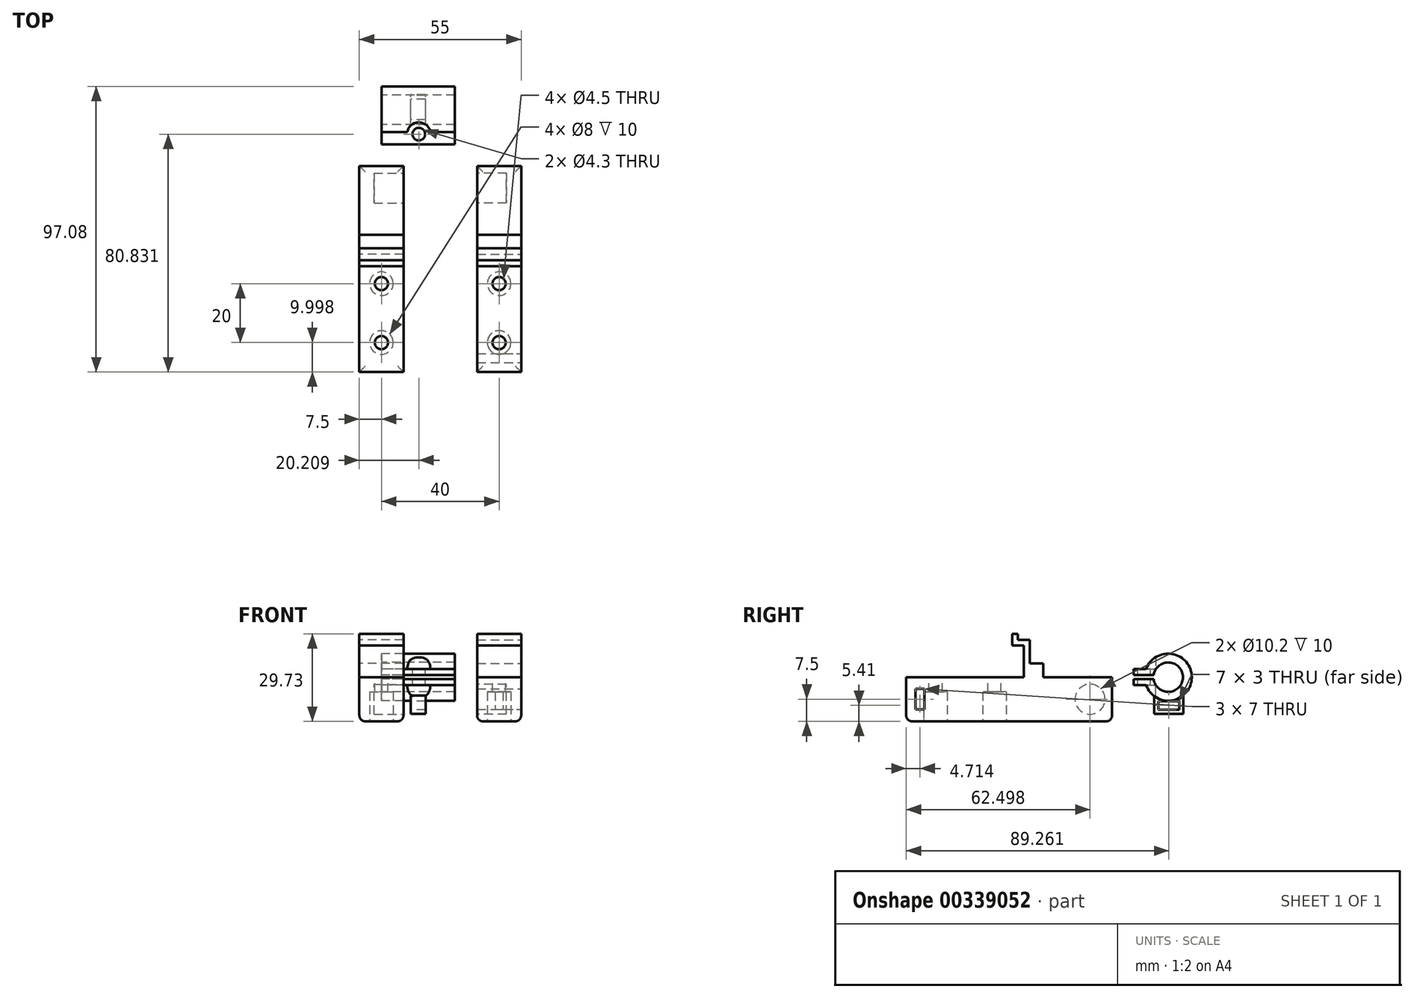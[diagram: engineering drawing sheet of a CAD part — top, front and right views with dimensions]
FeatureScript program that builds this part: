
annotation { "Feature Type Name" : "Feature", "Feature Type Description" : "" }
export const myFeature = defineFeature(function(context is Context, id is Id, definition is map)
    precondition{}
    {
        {
            var Q0;
            Q0=qCreatedBy(makeId("Top.planeOp"),FACE);
            var sketch = newSketch(context, id + "F0", { "sketchPlane" : qUnion([Q0])});
            skLineSegment(sketch, "E0", {"start": v(120.64, 20) * mm, "end": v(-98.83, 20) * mm, "construction": true});
            skLineSegment(sketch, "E1", {"start": v(-113.57, -20) * mm, "end": v(119.85, -20) * mm, "construction": true});
            skLineSegment(sketch, "E2", {"start": v(-15.81, 35.6) * mm, "end": v(120.22, 35.6) * mm, "construction": true});
            skLineSegment(sketch, "E3", {"start": v(0, 0) * mm, "end": v(121.2, 0) * mm, "construction": true});
            skSolve(sketch);
        }
        {
            var Q0;
            Q0=qCreatedBy(makeId("Right.planeOp"),FACE);
            var sketch = newSketch(context, id + "F1", { "sketchPlane" : qUnion([Q0])});
            skLineSegment(sketch, "E4", {"start": v(13.49, 0) * mm, "end": v(-26.51, 0) * mm});
            skLineSegment(sketch, "E5", {"start": v(-26.51, 0) * mm, "end": v(-26.51, -15) * mm});
            skLineSegment(sketch, "E6", {"start": v(-26.51, -15) * mm, "end": v(18.49, -15) * mm});
            skLineSegment(sketch, "E7", {"start": v(13.49, 10.73) * mm, "end": v(13.49, 0) * mm});
            skLineSegment(sketch, "E8", {"start": v(43.49, -15) * mm, "end": v(43.49, 0) * mm});
            skLineSegment(sketch, "E9", {"start": v(43.49, 0) * mm, "end": v(20.14, 0) * mm});
            skLineSegment(sketch, "E10", {"start": v(13.49, 10.73) * mm, "end": v(9.49, 10.73) * mm});
            skLineSegment(sketch, "E11", {"start": v(9.49, 10.73) * mm, "end": v(9.49, 14.73) * mm});
            skLineSegment(sketch, "E12", {"start": v(9.49, 14.73) * mm, "end": v(11.49, 14.73) * mm});
            skLineSegment(sketch, "E13", {"start": v(11.49, 14.73) * mm, "end": v(11.49, 12.73) * mm});
            skLineSegment(sketch, "E14", {"start": v(18.49, -15) * mm, "end": v(43.49, -15) * mm});
            skLineSegment(sketch, "E15", {"start": v(20.14, 0) * mm, "end": v(20.14, 4.7) * mm});
            skLineSegment(sketch, "E16", {"start": v(20.14, 4.7) * mm, "end": v(15.49, 4.7) * mm});
            skPoint(sketch, "E17.orphan", {"position": v(15.49, 0) * mm});
            skPoint(sketch, "E18.end.orphan", {"position": v(13.49, 21.47) * mm});
            skLineSegment(sketch, "E19", {"start": v(15.49, 4.7) * mm, "end": v(15.49, 12.7) * mm});
            skPoint(sketch, "E20.end.orphan", {"position": v(13.49, 12) * mm});
            skLineSegment(sketch, "E21", {"start": v(15.49, 12.7) * mm, "end": v(11.49, 12.73) * mm});
            skSolve(sketch);
        }
        {
            var Q0;
            Q0=makeQuery(id+"F1.imprint","IMPRINT",FACE,{"disambiguationData":[TD([[makeQuery(id+"F1.imprint","IMPRINT",EDGE,{"derivedFrom":sQuery(id+"F1.wireOp",EDGE,"E4")}),1.0]])]});
            var Q1;
            {var subQ0=sQuery(id+"F1.wireOp",EDGE,"E10");Q1=makeQuery(id+"F1.imprint","IMPRINT",FACE,{"disambiguationData":[TD([[makeQuery(id+"F1.imprint","IMPRINT",EDGE,{"derivedFrom":subQ0}),-1.0]])]});}
            extrude(context, id + "F2", {"entities" : qUnion([Q0, Q1]), "endBound" : BoundingType.SYMMETRIC, "depth" : 15 * mm});
        }
        {
            var Q0;
            Q0=makeQuery(id+"F2.opExtrude","CAP_FACE",FACE,{"disambiguationData":[OSD([sQuery(id+"F1.wireOp",EDGE,"E4"),sQuery(id+"F1.wireOp",EDGE,"E5"),sQuery(id+"F1.wireOp",EDGE,"E6"),sQuery(id+"F1.wireOp",EDGE,"E7"),sQuery(id+"F1.wireOp",EDGE,"E8"),sQuery(id+"F1.wireOp",EDGE,"E9"),sQuery(id+"F1.wireOp",EDGE,"E10"),sQuery(id+"F1.wireOp",EDGE,"E11"),sQuery(id+"F1.wireOp",EDGE,"E12"),sQuery(id+"F1.wireOp",EDGE,"E13"),sQuery(id+"F1.wireOp",EDGE,"E14"),sQuery(id+"F1.wireOp",EDGE,"E15"),sQuery(id+"F1.wireOp",EDGE,"E16"),sQuery(id+"F1.wireOp",EDGE,"E19"),sQuery(id+"F1.wireOp",EDGE,"E21")])],"isStart":false});
            var sketch = newSketch(context, id + "F3", { "sketchPlane" : qUnion([Q0])});
            skCircle(sketch, "E22", {"center": v(35.99, -7.5) * mm, "radius": 5.1 * mm});
            skSolve(sketch);
        }
        {
            var Q0;
            Q0=makeQuery(id+"F3.imprint","IMPRINT",FACE,{"disambiguationData":[TD([[makeQuery(id+"F3.imprint","IMPRINT",EDGE,{"derivedFrom":sQuery(id+"F3.wireOp",EDGE,"E22")}),1.0]])]});
            extrude(context, id + "F4", {"entities" : qUnion([Q0]), "operationType" : NewBodyOperationType.REMOVE, "oppositeDirection" : true, "depth" : 10 * mm});
        }
        {
            var Q0;
            Q0=qCreatedBy(makeId("Right.planeOp"),FACE);
            cPlane(context, id + "F5", {"entities" : qUnion([Q0]), "cplaneType" : CPlaneType.OFFSET, "offset" : 20 * mm, "width" : 150 * mm, "height" : 150 * mm});
        }
        {
            var Q0;
            Q0=makeQuery(id+"F2.opExtrude","SWEPT_BODY",BODY,{"disambiguationData":[OSD([sQuery(id+"F1.wireOp",EDGE,"E4"),sQuery(id+"F1.wireOp",EDGE,"E5"),sQuery(id+"F1.wireOp",EDGE,"E6"),sQuery(id+"F1.wireOp",EDGE,"E7"),sQuery(id+"F1.wireOp",EDGE,"E8"),sQuery(id+"F1.wireOp",EDGE,"E9"),sQuery(id+"F1.wireOp",EDGE,"E10"),sQuery(id+"F1.wireOp",EDGE,"E11"),sQuery(id+"F1.wireOp",EDGE,"E12"),sQuery(id+"F1.wireOp",EDGE,"E13"),sQuery(id+"F1.wireOp",EDGE,"E14"),sQuery(id+"F1.wireOp",EDGE,"E15"),sQuery(id+"F1.wireOp",EDGE,"E16"),sQuery(id+"F1.wireOp",EDGE,"E19"),sQuery(id+"F1.wireOp",EDGE,"E21")])]});
            var Q1;
            Q1=qCreatedBy(id+"F5.planeOp",FACE);
            mirror(context, id + "F6", {"entities" : qUnion([Q0]), "mirrorPlane" : qUnion([Q1])});
        }
        {
            var Q0;
            Q0=makeQuery(id+"F6.opPattern","COPY",FACE,{"derivedFrom":makeQuery(id+"F2.opExtrude","CAP_FACE",FACE,{"disambiguationData":[OSD([sQuery(id+"F1.wireOp",EDGE,"E4"),sQuery(id+"F1.wireOp",EDGE,"E5"),sQuery(id+"F1.wireOp",EDGE,"E6"),sQuery(id+"F1.wireOp",EDGE,"E7"),sQuery(id+"F1.wireOp",EDGE,"E8"),sQuery(id+"F1.wireOp",EDGE,"E9"),sQuery(id+"F1.wireOp",EDGE,"E10"),sQuery(id+"F1.wireOp",EDGE,"E11"),sQuery(id+"F1.wireOp",EDGE,"E12"),sQuery(id+"F1.wireOp",EDGE,"E13"),sQuery(id+"F1.wireOp",EDGE,"E14"),sQuery(id+"F1.wireOp",EDGE,"E15"),sQuery(id+"F1.wireOp",EDGE,"E16"),sQuery(id+"F1.wireOp",EDGE,"E19"),sQuery(id+"F1.wireOp",EDGE,"E21")])],"isStart":true}),"instanceName":"1"});
            var sketch = newSketch(context, id + "F7", { "sketchPlane" : qUnion([Q0])});
            skLineSegment(sketch, "E23.bottom", {"start": v(-20.3, -4) * mm, "end": v(-23.3, -4) * mm});
            skLineSegment(sketch, "E23.top", {"start": v(-20.3, -11) * mm, "end": v(-23.3, -11) * mm});
            skLineSegment(sketch, "E23.left", {"start": v(-20.3, -4) * mm, "end": v(-20.3, -11) * mm});
            skLineSegment(sketch, "E23.right", {"start": v(-23.3, -4) * mm, "end": v(-23.3, -11) * mm});
            skSolve(sketch);
        }
        {
            var Q0;
            Q0=makeQuery(id+"F7.imprint","IMPRINT",FACE,{"disambiguationData":[TD([[makeQuery(id+"F7.imprint","IMPRINT",EDGE,{"derivedFrom":sQuery(id+"F7.wireOp",EDGE,"E23.bottom")}),1.0]])]});
            extrude(context, id + "F8", {"entities" : qUnion([Q0]), "operationType" : NewBodyOperationType.REMOVE, "endBound" : BoundingType.UP_TO_NEXT, "oppositeDirection" : true, "depth" : 25 * mm});
        }
        {
            var Q0;
            Q0=makeQuery(id+"F8.boolean.opBoolean","COPY",EDGE,{"derivedFrom":makeQuery(id+"F8.opExtrude","CAP_EDGE",EDGE,{"disambiguationData":[OSD([sQuery(id+"F7.wireOp",EDGE,"E23.right")])],"isStart":true})});
            var Q1;
            Q1=makeQuery(id+"F8.boolean.opBoolean","COPY",EDGE,{"derivedFrom":makeQuery(id+"F8.opExtrude","TWEAK_EDGE",EDGE,{"derivedFrom":[makeQuery(id+"F6.opPattern","COPY",FACE,{"derivedFrom":makeQuery(id+"F2.opExtrude","CAP_FACE",FACE,{"disambiguationData":[OSD([sQuery(id+"F1.wireOp",EDGE,"E4"),sQuery(id+"F1.wireOp",EDGE,"E5"),sQuery(id+"F1.wireOp",EDGE,"E6"),sQuery(id+"F1.wireOp",EDGE,"E7"),sQuery(id+"F1.wireOp",EDGE,"E8"),sQuery(id+"F1.wireOp",EDGE,"E9"),sQuery(id+"F1.wireOp",EDGE,"E10"),sQuery(id+"F1.wireOp",EDGE,"E11"),sQuery(id+"F1.wireOp",EDGE,"E12"),sQuery(id+"F1.wireOp",EDGE,"E13"),sQuery(id+"F1.wireOp",EDGE,"E14"),sQuery(id+"F1.wireOp",EDGE,"E15"),sQuery(id+"F1.wireOp",EDGE,"E16"),sQuery(id+"F1.wireOp",EDGE,"E19"),sQuery(id+"F1.wireOp",EDGE,"E21")])],"isStart":false}),"instanceName":"1"}),makeQuery(id+"F7.imprint","IMPRINT",EDGE,{"derivedFrom":sQuery(id+"F7.wireOp",EDGE,"E23.right")})]})});
            var Q2;
            Q2=makeQuery(id+"F6.opPattern","COPY",EDGE,{"derivedFrom":makeQuery(id+"F2.opExtrude","CAP_EDGE",EDGE,{"disambiguationData":[OSD([sQuery(id+"F1.wireOp",EDGE,"E6"),sQuery(id+"F1.wireOp",EDGE,"E14")])],"isStart":false}),"instanceName":"1"});
            var Q3;
            Q3=makeQuery(id+"F6.opPattern","COPY",EDGE,{"derivedFrom":makeQuery(id+"F2.opExtrude","CAP_EDGE",EDGE,{"disambiguationData":[OSD([sQuery(id+"F1.wireOp",EDGE,"E6"),sQuery(id+"F1.wireOp",EDGE,"E14")])],"isStart":true}),"instanceName":"1"});
            var Q4;
            Q4=makeQuery(id+"F2.opExtrude","CAP_EDGE",EDGE,{"disambiguationData":[OSD([sQuery(id+"F1.wireOp",EDGE,"E6"),sQuery(id+"F1.wireOp",EDGE,"E14")])],"isStart":true});
            var Q5;
            Q5=makeQuery(id+"F2.opExtrude","CAP_EDGE",EDGE,{"disambiguationData":[OSD([sQuery(id+"F1.wireOp",EDGE,"E6"),sQuery(id+"F1.wireOp",EDGE,"E14")])],"isStart":false});
            var Q6;
            Q6=makeQuery(id+"F6.opPattern","COPY",EDGE,{"derivedFrom":makeQuery(id+"F2.opExtrude","SWEPT_EDGE",EDGE,{"disambiguationData":[OSD([sQuery(id+"F1.wireOp",EDGE,"E5"),sQuery(id+"F1.wireOp",EDGE,"E6")])]}),"instanceName":"1"});
            var Q7;
            Q7=makeQuery(id+"F2.opExtrude","SWEPT_EDGE",EDGE,{"disambiguationData":[OSD([sQuery(id+"F1.wireOp",EDGE,"E5"),sQuery(id+"F1.wireOp",EDGE,"E6")])]});
            var Q8;
            Q8=makeQuery(id+"F2.opExtrude","SWEPT_EDGE",EDGE,{"disambiguationData":[OSD([sQuery(id+"F1.wireOp",EDGE,"E8"),sQuery(id+"F1.wireOp",EDGE,"E14")])]});
            var Q9;
            Q9=makeQuery(id+"F6.opPattern","COPY",EDGE,{"derivedFrom":makeQuery(id+"F2.opExtrude","SWEPT_EDGE",EDGE,{"disambiguationData":[OSD([sQuery(id+"F1.wireOp",EDGE,"E8"),sQuery(id+"F1.wireOp",EDGE,"E14")])]}),"instanceName":"1"});
            fillet(context, id + "F9", {"entities" : qUnion([Q0, Q1, Q2, Q3, Q4, Q5, Q6, Q7, Q8, Q9]), "radius" : 2 * mm, "tangentPropagation" : true, "allowEdgeOverflow" : false});
        }
        {
            var Q0;
            Q0=makeQuery(id+"F2.opExtrude","SWEPT_FACE",FACE,{"disambiguationData":[OSD([sQuery(id+"F1.wireOp",EDGE,"E4")])]});
            var sketch = newSketch(context, id + "F10", { "sketchPlane" : qUnion([Q0])});
            skCircle(sketch, "E24", {"center": v(0, 3.49) * mm, "radius": 2.25 * mm});
            skCircle(sketch, "E25", {"center": v(0, -16.51) * mm, "radius": 2.25 * mm});
            skSolve(sketch);
        }
        {
            var Q0;
            Q0=makeQuery(id+"F10.imprint","IMPRINT",FACE,{"disambiguationData":[TD([[makeQuery(id+"F10.imprint","IMPRINT",EDGE,{"derivedFrom":sQuery(id+"F10.wireOp",EDGE,"E24")}),1.0]])]});
            var Q1;
            Q1=makeQuery(id+"F10.imprint","IMPRINT",FACE,{"disambiguationData":[TD([[makeQuery(id+"F10.imprint","IMPRINT",EDGE,{"derivedFrom":sQuery(id+"F10.wireOp",EDGE,"E25")}),1.0]])]});
            var Q2;
            Q2=sQuery(id+"F10.wireOp",EDGE,"E24");
            var Q3;
            Q3=sQuery(id+"F10.wireOp",EDGE,"E25");
            extrude(context, id + "F11", {"entities" : qUnion([Q0, Q1]), "operationType" : NewBodyOperationType.REMOVE, "surfaceEntities" : qUnion([Q2, Q3]), "endBound" : BoundingType.UP_TO_NEXT, "oppositeDirection" : true, "depth" : 25 * mm});
        }
        {
            var Q0;
            Q0=makeQuery(id+"F6.opPattern","COPY",FACE,{"derivedFrom":makeQuery(id+"F2.opExtrude","SWEPT_FACE",FACE,{"disambiguationData":[OSD([sQuery(id+"F1.wireOp",EDGE,"E4")])]}),"instanceName":"1"});
            var sketch = newSketch(context, id + "F12", { "sketchPlane" : qUnion([Q0])});
            skCircle(sketch, "E26", {"center": v(40, 3.49) * mm, "radius": 2.25 * mm});
            skCircle(sketch, "E27", {"center": v(40, -16.51) * mm, "radius": 2.25 * mm});
            skSolve(sketch);
        }
        {
            var Q0;
            Q0=makeQuery(id+"F12.imprint","IMPRINT",FACE,{"disambiguationData":[TD([[makeQuery(id+"F12.imprint","IMPRINT",EDGE,{"derivedFrom":sQuery(id+"F12.wireOp",EDGE,"E26")}),1.0]])]});
            var Q1;
            Q1=makeQuery(id+"F12.imprint","IMPRINT",FACE,{"disambiguationData":[TD([[makeQuery(id+"F12.imprint","IMPRINT",EDGE,{"derivedFrom":sQuery(id+"F12.wireOp",EDGE,"E27")}),1.0]])]});
            extrude(context, id + "F13", {"entities" : qUnion([Q0, Q1]), "operationType" : NewBodyOperationType.REMOVE, "endBound" : BoundingType.UP_TO_NEXT, "oppositeDirection" : true, "depth" : 25 * mm});
        }
        {
            var Q0;
            Q0=makeQuery(id+"F6.opPattern","COPY",FACE,{"derivedFrom":makeQuery(id+"F2.opExtrude","SWEPT_FACE",FACE,{"disambiguationData":[OSD([sQuery(id+"F1.wireOp",EDGE,"E6"),sQuery(id+"F1.wireOp",EDGE,"E14")])]}),"instanceName":"1"});
            var sketch = newSketch(context, id + "F14", { "sketchPlane" : qUnion([Q0])});
            skCircle(sketch, "E28", {"center": v(40, -3.49) * mm, "radius": 4 * mm});
            skCircle(sketch, "E29", {"center": v(40, 16.51) * mm, "radius": 4 * mm});
            skSolve(sketch);
        }
        {
            var Q0;
            Q0=makeQuery(id+"F14.imprint","IMPRINT",FACE,{"disambiguationData":[TD([[makeQuery(id+"F14.imprint","IMPRINT",EDGE,{"derivedFrom":sQuery(id+"F14.wireOp",EDGE,"E28")}),1.0]])]});
            var Q1;
            Q1=makeQuery(id+"F14.imprint","IMPRINT",FACE,{"disambiguationData":[TD([[makeQuery(id+"F14.imprint","IMPRINT",EDGE,{"derivedFrom":sQuery(id+"F14.wireOp",EDGE,"E29")}),1.0]])]});
            extrude(context, id + "F15", {"entities" : qUnion([Q0, Q1]), "operationType" : NewBodyOperationType.REMOVE, "oppositeDirection" : true, "depth" : 10 * mm});
        }
        {
            var Q0;
            Q0=makeQuery(id+"F2.opExtrude","SWEPT_FACE",FACE,{"disambiguationData":[OSD([sQuery(id+"F1.wireOp",EDGE,"E6"),sQuery(id+"F1.wireOp",EDGE,"E14")])]});
            var sketch = newSketch(context, id + "F16", { "sketchPlane" : qUnion([Q0])});
            skCircle(sketch, "E30", {"center": v(0, -3.49) * mm, "radius": 4 * mm});
            skCircle(sketch, "E31", {"center": v(0, 16.51) * mm, "radius": 4 * mm});
            skSolve(sketch);
        }
        {
            var Q0;
            Q0=makeQuery(id+"F16.imprint","IMPRINT",FACE,{"disambiguationData":[TD([[makeQuery(id+"F16.imprint","IMPRINT",EDGE,{"derivedFrom":sQuery(id+"F16.wireOp",EDGE,"E30")}),1.0]])]});
            var Q1;
            Q1=makeQuery(id+"F16.imprint","IMPRINT",FACE,{"disambiguationData":[TD([[makeQuery(id+"F16.imprint","IMPRINT",EDGE,{"derivedFrom":sQuery(id+"F16.wireOp",EDGE,"E31")}),1.0]])]});
            extrude(context, id + "F17", {"entities" : qUnion([Q0, Q1]), "operationType" : NewBodyOperationType.REMOVE, "oppositeDirection" : true, "depth" : 10 * mm});
        }
        {
            var Q0;
            Q0=qCreatedBy(makeId("Right.planeOp"),FACE);
            var sketch = newSketch(context, id + "F18", { "sketchPlane" : qUnion([Q0])});
            skArc(sketch, "E32", {"start": v(57.63, -0.71) * mm, "mid": v(67.57, 0) * mm, "end": v(57.63, 0.71) * mm});
            skArc(sketch, "E33", {"start": v(55.05, -2.71) * mm, "mid": v(70.57, 0) * mm, "end": v(55.05, 2.71) * mm});
            skLineSegment(sketch, "E34", {"start": v(57.63, -0.71) * mm, "end": v(54.6, -0.71) * mm});
            skLineSegment(sketch, "E35.MirrorCS", {"start": v(57.63, 0.71) * mm, "end": v(54.6, 0.71) * mm});
            skLineSegment(sketch, "E36.bottom", {"start": v(57.63, 0.71) * mm, "end": v(50.84, 0.71) * mm});
            skLineSegment(sketch, "E36.top", {"start": v(55.05, 2.71) * mm, "end": v(50.84, 2.71) * mm});
            skLineSegment(sketch, "E36.right", {"start": v(50.84, 0.71) * mm, "end": v(50.84, 2.71) * mm});
            skLineSegment(sketch, "E37.MirrorCS", {"start": v(55.05, -2.71) * mm, "end": v(50.84, -2.71) * mm});
            skLineSegment(sketch, "E38.MirrorCS", {"start": v(50.84, -0.71) * mm, "end": v(50.84, -2.71) * mm});
            skLineSegment(sketch, "E39.MirrorCS", {"start": v(57.63, -0.71) * mm, "end": v(50.84, -0.71) * mm});
            skPoint(sketch, "E40.orphan", {"position": v(57.63, -2.71) * mm});
            skPoint(sketch, "E41.MirrorCS.start.orphan", {"position": v(57.63, -0.71) * mm});
            skPoint(sketch, "E36.left.end.orphan", {"position": v(57.63, 2.71) * mm});
            skSolve(sketch);
        }
        {
            var Q0;
            {var subQ3=sQuery(id+"F18.wireOp",EDGE,"E32");Q0=makeQuery(id+"F18.imprint","IMPRINT",FACE,{"disambiguationData":[TD([[makeQuery(id+"F18.imprint","IMPRINT",EDGE,{"derivedFrom":subQ3}),-1.0]])]});}
            extrude(context, id + "F19", {"entities" : qUnion([Q0]), "depth" : 25 * mm});
        }
        {
            var Q0;
            Q0=qCreatedBy(makeId("Top.planeOp"),FACE);
            var sketch = newSketch(context, id + "F20", { "sketchPlane" : qUnion([Q0])});
            skCircle(sketch, "E42", {"center": v(12.7, 54.32) * mm, "radius": 2.15 * mm});
            skSolve(sketch);
        }
        {
            var Q0;
            Q0=qSketchRegion(id+"F20",true);
            var Q1;
            Q1=sQuery(id+"F20.wireOp",EDGE,"E42");
            extrude(context, id + "F21", {"entities" : qUnion([Q0]), "operationType" : NewBodyOperationType.REMOVE, "surfaceEntities" : qUnion([Q1]), "endBound" : BoundingType.SYMMETRIC, "oppositeDirection" : true, "depth" : 25 * mm});
        }
        {
            var Q0;
            Q0=makeQuery(id+"F19.opExtrude","SWEPT_FACE",FACE,{"disambiguationData":[OSD([sQuery(id+"F18.wireOp",EDGE,"E37.MirrorCS")])]});
            var sketch = newSketch(context, id + "F22", { "sketchPlane" : qUnion([Q0])});
            skCircle(sketch, "E43", {"center": v(12.7, -54.32) * mm, "radius": 4 * mm});
            skSolve(sketch);
        }
        {
            var Q0;
            Q0=qSketchRegion(id+"F22",true);
            extrude(context, id + "F23", {"entities" : qUnion([Q0]), "operationType" : NewBodyOperationType.REMOVE, "depth" : 25 * mm});
        }
        {
            var Q0;
            Q0=makeQuery(id+"F19.opExtrude","SWEPT_FACE",FACE,{"disambiguationData":[OSD([sQuery(id+"F18.wireOp",EDGE,"E36.top")])]});
            var sketch = newSketch(context, id + "F24", { "sketchPlane" : qUnion([Q0])});
            skCircle(sketch, "E44", {"center": v(12.7, 54.32) * mm, "radius": 4 * mm});
            skSolve(sketch);
        }
        {
            var Q0;
            Q0=qSketchRegion(id+"F24",true);
            extrude(context, id + "F25", {"entities" : qUnion([Q0]), "operationType" : NewBodyOperationType.REMOVE, "depth" : 25 * mm});
        }
        {
            var Q0;
            Q0=qCreatedBy(makeId("Right.planeOp"),FACE);
            cPlane(context, id + "F26", {"entities" : qUnion([Q0]), "cplaneType" : CPlaneType.OFFSET, "offset" : 12.5 * mm, "width" : 150 * mm, "height" : 150 * mm});
        }
        {
            var Q0;
            Q0=qCreatedBy(id+"F26.planeOp",FACE);
            var sketch = newSketch(context, id + "F27", { "sketchPlane" : qUnion([Q0])});
            skLineSegment(sketch, "E45.bottom", {"start": v(57.76, -6.3) * mm, "end": v(57.75, -12.5) * mm});
            skLineSegment(sketch, "E45.left", {"start": v(57.76, -6.3) * mm, "end": v(62.76, -6.3) * mm});
            skLineSegment(sketch, "E46.MirrorCS", {"start": v(67.76, -6.3) * mm, "end": v(67.76, -12.5) * mm});
            skLineSegment(sketch, "E47.MirrorCS", {"start": v(67.76, -6.3) * mm, "end": v(62.76, -6.3) * mm});
            skLineSegment(sketch, "E48", {"start": v(57.75, -12.5) * mm, "end": v(67.76, -12.5) * mm});
            skLineSegment(sketch, "E49.bottom", {"start": v(59.25, -11.09) * mm, "end": v(59.25, -8.09) * mm});
            skLineSegment(sketch, "E49.top", {"start": v(66.25, -11.09) * mm, "end": v(66.25, -8.09) * mm});
            skLineSegment(sketch, "E49.left", {"start": v(59.25, -11.09) * mm, "end": v(66.25, -11.09) * mm});
            skLineSegment(sketch, "E49.right", {"start": v(59.25, -8.09) * mm, "end": v(66.25, -8.09) * mm});
            skSolve(sketch);
        }
        {
            var Q0;
            Q0=qSketchRegion(id+"F27",true);
            extrude(context, id + "F28", {"entities" : qUnion([Q0]), "operationType" : NewBodyOperationType.ADD, "endBound" : BoundingType.SYMMETRIC, "depth" : 5 * mm});
        }
    });
